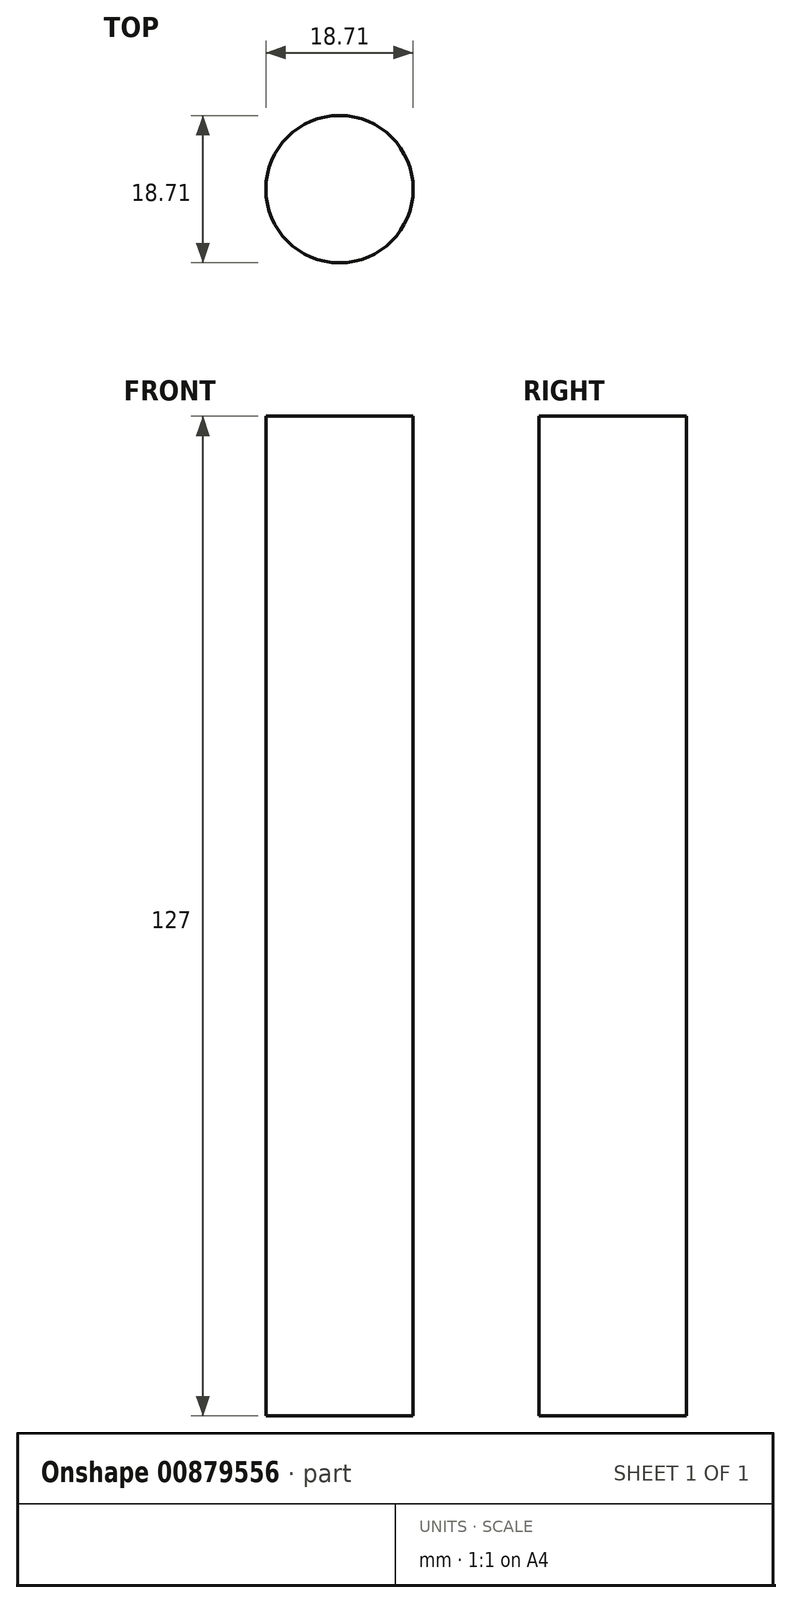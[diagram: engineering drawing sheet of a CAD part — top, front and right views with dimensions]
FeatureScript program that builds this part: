
annotation { "Feature Type Name" : "Feature", "Feature Type Description" : "" }
export const myFeature = defineFeature(function(context is Context, id is Id, definition is map)
    precondition{}
    {
        {
            var Q0;
            Q0=qCreatedBy(makeId("Top.planeOp"),FACE);
            var sketch = newSketch(context, id + "F0", { "sketchPlane" : qUnion([Q0])});
            skCircle(sketch, "E0", {"center": v(-60.75, -35.5) * mm, "radius": 9.36 * mm});
            skSolve(sketch);
        }
        {
            var Q0;
            Q0 = qSketchRegion(id + "F0", true);
            extrude(context, id + "F1", {"entities" : qUnion([Q0]), "depth" : 127 * mm, "offsetDistance" : 25.4 * mm});
        }
    });
